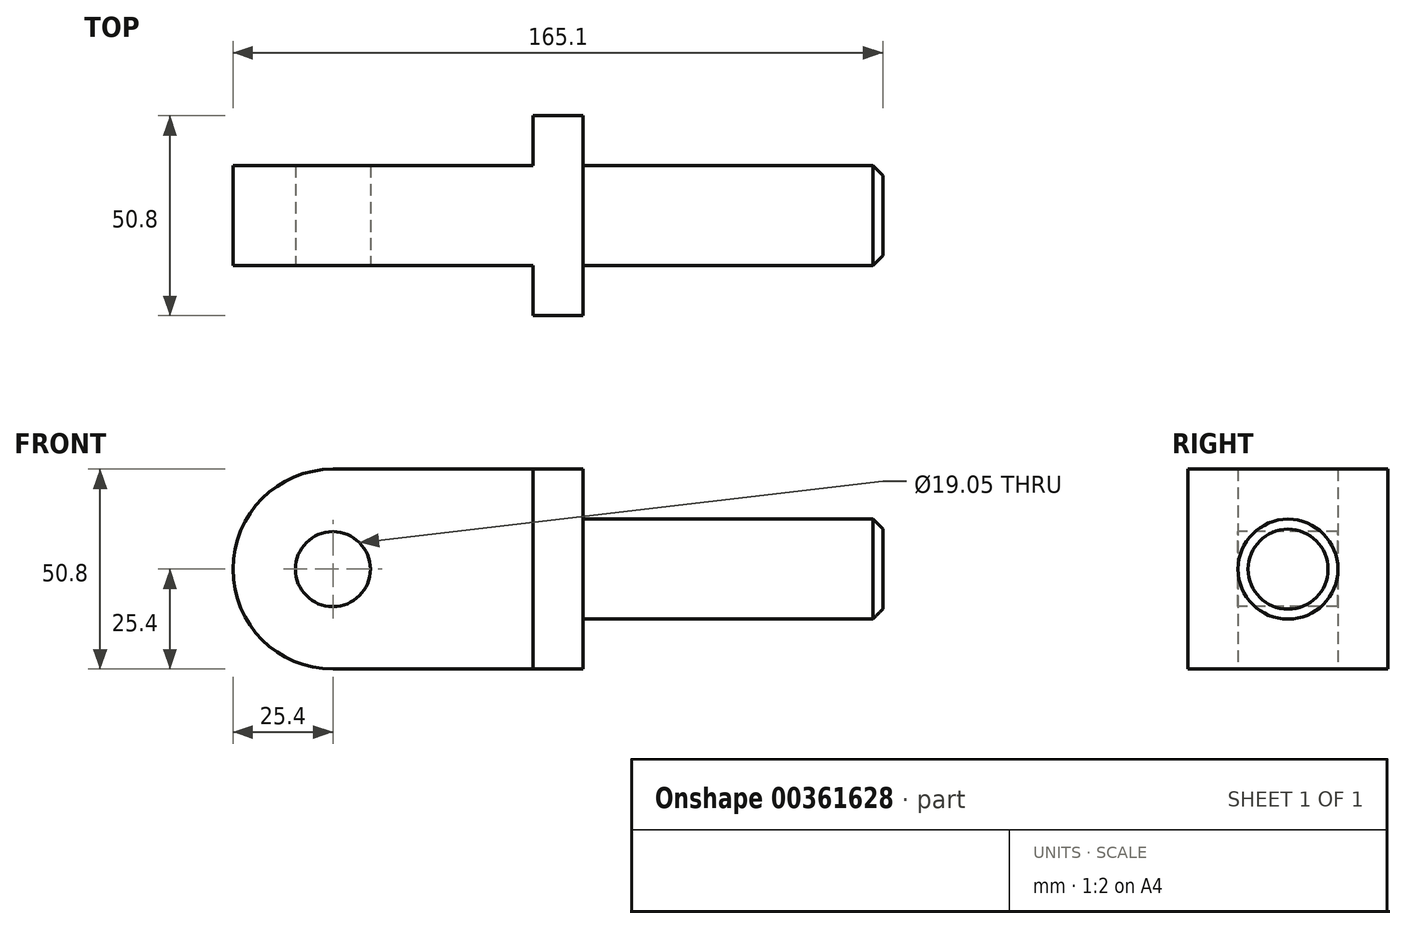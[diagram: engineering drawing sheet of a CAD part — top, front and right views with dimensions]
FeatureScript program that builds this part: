
annotation { "Feature Type Name" : "Feature", "Feature Type Description" : "" }
export const myFeature = defineFeature(function(context is Context, id is Id, definition is map)
    precondition{}
    {
        {
            var Q0;
            Q0=qCreatedBy(makeId("Right.planeOp"),FACE);
            var sketch = newSketch(context, id + "F0", { "sketchPlane" : qUnion([Q0])});
            skLineSegment(sketch, "E0.bottom", {"start": v(0, 0) * mm, "end": v(50.8, 0) * mm});
            skLineSegment(sketch, "E0.top", {"start": v(0, 50.8) * mm, "end": v(50.8, 50.8) * mm});
            skLineSegment(sketch, "E0.left", {"start": v(0, 0) * mm, "end": v(0, 50.8) * mm});
            skLineSegment(sketch, "E0.right", {"start": v(50.8, 0) * mm, "end": v(50.8, 50.8) * mm});
            skSolve(sketch);
        }
        {
            var Q0;
            Q0 = qSketchRegion(id + "F0", true);
            extrude(context, id + "F1", {"entities" : qUnion([Q0]), "depth" : 12.7 * mm});
        }
        {
            var Q0;
            Q0=makeQuery(id+"F1.opExtrude","CAP_FACE",FACE,{"disambiguationData":[OSD([sQuery(id+"F0.wireOp",EDGE,"E0.bottom"),sQuery(id+"F0.wireOp",EDGE,"E0.top"),sQuery(id+"F0.wireOp",EDGE,"E0.left"),sQuery(id+"F0.wireOp",EDGE,"E0.right")])],"isStart":false});
            var sketch = newSketch(context, id + "F2", { "sketchPlane" : qUnion([Q0])});
            skCircle(sketch, "E1", {"center": v(25.4, 25.4) * mm, "radius": 12.7 * mm});
            skSolve(sketch);
        }
        {
            var Q0;
            Q0 = qSketchRegion(id + "F2", true);
            extrude(context, id + "F3", {"entities" : qUnion([Q0]), "operationType" : NewBodyOperationType.ADD, "depth" : 76.2 * mm});
        }
        {
            var Q0;
            Q0=makeQuery(id+"F3.opExtrude","CAP_EDGE",EDGE,{"disambiguationData":[OSD([sQuery(id+"F2.wireOp",EDGE,"E1")])],"isStart":false});
            chamfer(context, id + "F4", {"entities" : qUnion([Q0]), "width" : 2.54 * mm, "tangentPropagation" : true});
        }
        {
            var Q0;
            Q0=makeQuery(id+"F1.opExtrude","CAP_FACE",FACE,{"disambiguationData":[OSD([sQuery(id+"F0.wireOp",EDGE,"E0.bottom"),sQuery(id+"F0.wireOp",EDGE,"E0.top"),sQuery(id+"F0.wireOp",EDGE,"E0.left"),sQuery(id+"F0.wireOp",EDGE,"E0.right")])],"isStart":true});
            var sketch = newSketch(context, id + "F5", { "sketchPlane" : qUnion([Q0])});
            skLineSegment(sketch, "E2.bottom", {"start": v(-38.1, 50.8) * mm, "end": v(-12.7, 50.8) * mm});
            skLineSegment(sketch, "E2.top", {"start": v(-38.1, 0) * mm, "end": v(-12.7, 0) * mm});
            skLineSegment(sketch, "E2.left", {"start": v(-38.1, 50.8) * mm, "end": v(-38.1, 0) * mm});
            skLineSegment(sketch, "E2.right", {"start": v(-12.7, 50.8) * mm, "end": v(-12.7, 0) * mm});
            skLineSegment(sketch, "E3", {"start": v(-25.4, 50.8) * mm, "end": v(-25.4, 0) * mm, "construction": true});
            skSolve(sketch);
        }
        {
            var Q0;
            Q0 = qSketchRegion(id + "F5", true);
            extrude(context, id + "F6", {"entities" : qUnion([Q0]), "operationType" : NewBodyOperationType.ADD, "depth" : 76.2 * mm});
        }
        {
            var Q0;
            Q0=makeQuery(id+"F6.opExtrude","SWEPT_FACE",FACE,{"disambiguationData":[OSD([sQuery(id+"F5.wireOp",EDGE,"E2.right")])]});
            var sketch = newSketch(context, id + "F7", { "sketchPlane" : qUnion([Q0])});
            skLineSegment(sketch, "E4", {"start": v(-50.8, 50.8) * mm, "end": v(-76.2, 50.8) * mm});
            skLineSegment(sketch, "E5", {"start": v(-76.2, 50.8) * mm, "end": v(-76.2, 0) * mm});
            skLineSegment(sketch, "E6", {"start": v(-50.8, 0) * mm, "end": v(-76.2, 0) * mm});
            skArc(sketch, "E7", {"start": v(-50.8, 50.8) * mm, "mid": v(-76.2, 25.4) * mm, "end": v(-50.8, 0) * mm});
            skCircle(sketch, "E8", {"center": v(-50.8, 25.4) * mm, "radius": 9.53 * mm});
            skSolve(sketch);
        }
        {
            var Q0;
            Q0 = qSketchRegion(id + "F7", true);
            extrude(context, id + "F8", {"entities" : qUnion([Q0]), "operationType" : NewBodyOperationType.REMOVE, "endBound" : BoundingType.THROUGH_ALL, "oppositeDirection" : true, "depth" : 25.4 * mm});
        }
    });
